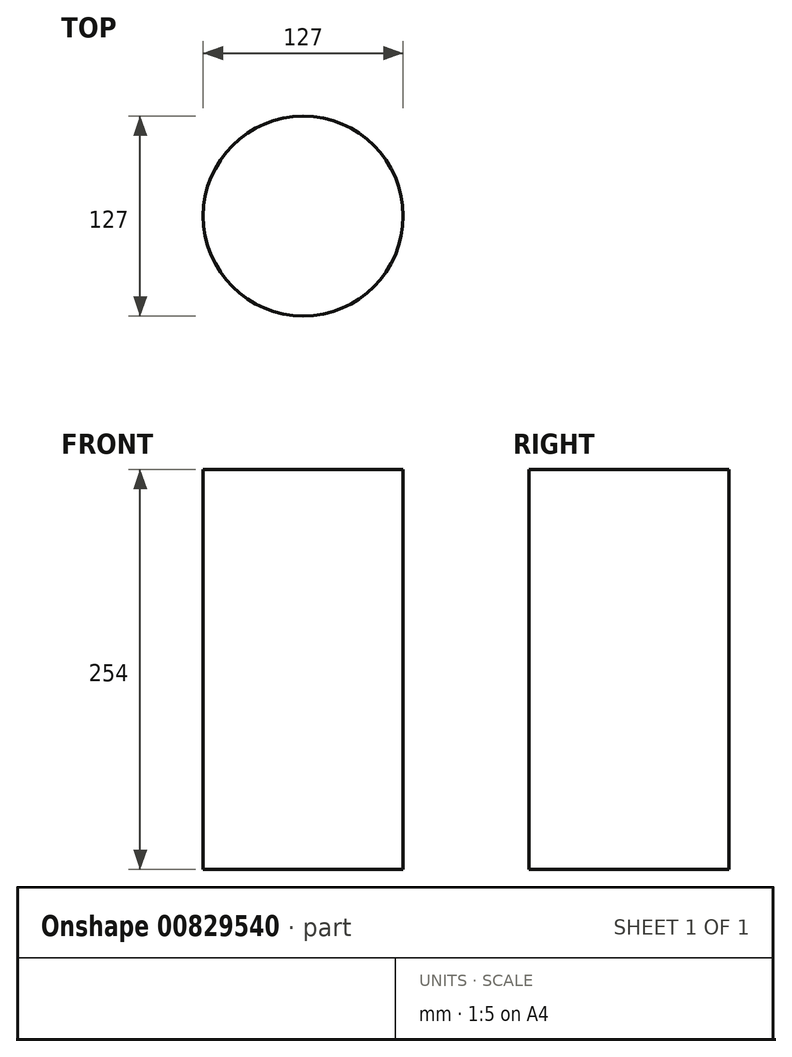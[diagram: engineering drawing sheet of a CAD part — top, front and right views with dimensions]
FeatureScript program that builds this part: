
annotation { "Feature Type Name" : "Feature", "Feature Type Description" : "" }
export const myFeature = defineFeature(function(context is Context, id is Id, definition is map)
    precondition{}
    {
        {
            var Q0;
            Q0=qCreatedBy(makeId("Top.planeOp"),FACE);
            var sketch = newSketch(context, id + "F0", { "sketchPlane" : qUnion([Q0])});
            skCircle(sketch, "E0", {"center": v(0, 0) * mm, "radius": 63.5 * mm});
            skSolve(sketch);
        }
        {
            var Q0;
            Q0=makeQuery(id+"F0.imprint","IMPRINT",FACE,{"disambiguationData":[TD([[makeQuery(id+"F0.imprint","IMPRINT",EDGE,{"derivedFrom":sQuery(id+"F0.wireOp",EDGE,"E0")}),1.0]])]});
            extrude(context, id + "F1", {"entities" : qUnion([Q0]), "depth" : 254 * mm, "offsetDistance" : 25.4 * mm});
        }
    });
